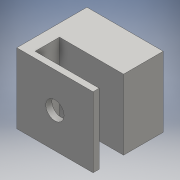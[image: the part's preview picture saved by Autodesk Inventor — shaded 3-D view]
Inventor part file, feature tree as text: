
AUTODESK INVENTOR PART (.ipt)
format: ipt  version: 2016 (Build 200138000, 138)  size: 99,840 bytes
history: native  units: mm
features: extrude x2, sketch x2
ambient origin geometry x8: Origin, YZ Plane, XZ Plane, XY Plane, X Axis, Y Axis, Z Axis, Center Point
bodies: Solid1 (feature_tree)
feature tree (4):
  extrude  "Extrusion1"  Depth=2.0mm
  extrude  "Extrusion2"  Depth=13.0mm
  sketch  "Sketch1"  dims[d0=25.0mm d1=2.0mm]
  sketch  "Sketch2"  dims[d2=8.0mm d5=13.0mm d6=23.0mm d7=0.0mm d8=6.0mm d9=23.0mm d10=0.0mm]
